# Revit family: Basketball_Backstop-Gared-9408-Portable-sat_Import
name_source: partatom
category: Specialty Equipment
revit_build: Autodesk Revit 2017 (Build: 20170816_0615(x64)
units: mm (PartAtom-declared; Revit-internal decimal feet)

## family parameters
Always vertical = Yes
Cut with Voids When Loaded = No
OmniClass Number = 23.40.50.34.14.11
OmniClass Title = Backstops
Part Type = Normal
Room Calculation Point = No
Round Connector Dimension = Use Diameter
Shared = No
Work Plane-Based = No

## types (1)
- Basketball_Backstop-Gared-9408-Portable-sat_Import
    Assembly Code = E1020900
    BIM Version = v3.1
    BIM Version Available (Earliest) = 2012
    CSI MasterFormat = 11 66 23
    Description = Portable Basketball Backstop - 9408 Hoopmaster 8
    Developer Note = This file contains a 3D .sat file import only.
    Manufacturer = Gared Sports
    Model = 9408
    Product Page URL = http://www.perfsports.com
    URL = http://www.garedsports.com

## geometry (parser evidence)
native form markers: Sweep x3
no freeform markers — native parametric forms only
